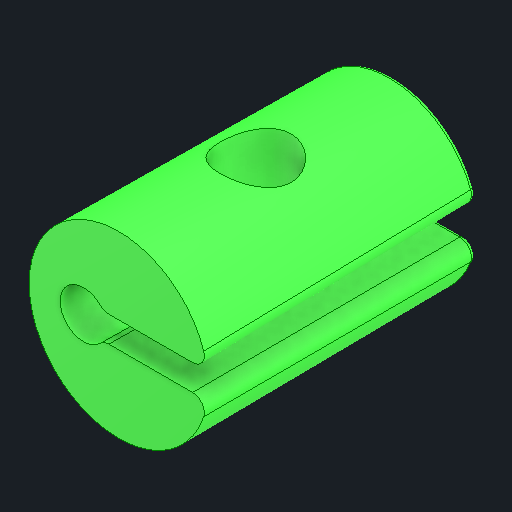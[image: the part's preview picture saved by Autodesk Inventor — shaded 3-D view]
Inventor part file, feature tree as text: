
AUTODESK INVENTOR PART (.ipt)
format: ipt  version: 2024 (Build 280153000, 153)  size: 200,192 bytes
history: native  units: in
note: dims shown in document units (in); Inventor stores cm internally (conversion verified against a paired STEP export)
features: fillet x1
ambient origin geometry x8: Origin, YZ Plane, XZ Plane, XY Plane, X Axis, Y Axis, Z Axis, Center Point
bodies: Solid1 (feature_tree)
feature tree (1):
  fillet  "Fillet2"  [1 undecoded]
note: 1 required parameter value undecoded (feature->parameter linkage not recoverable at this tier; creation-order binding heuristic only, values carry confidence <= 0.55)
